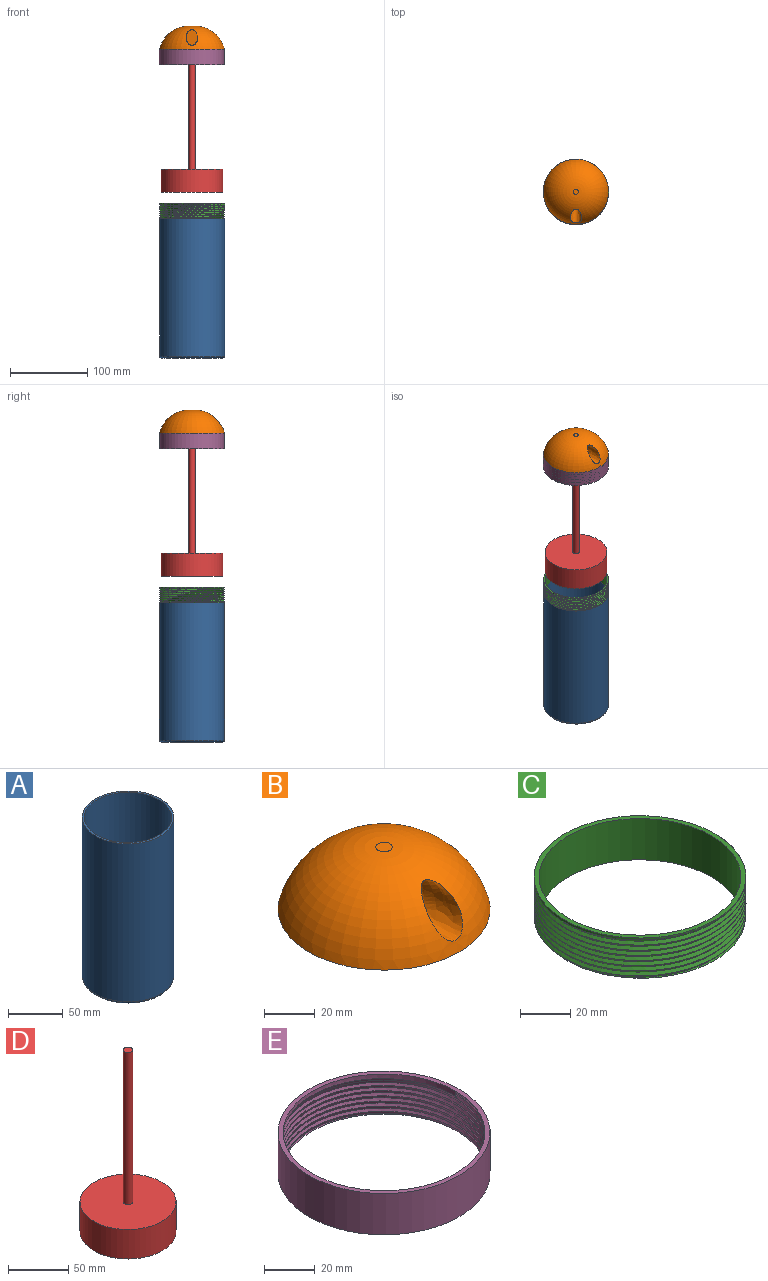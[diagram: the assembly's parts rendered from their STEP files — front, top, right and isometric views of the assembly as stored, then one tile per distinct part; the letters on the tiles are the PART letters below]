
ASSEMBLY  parts=5 mates=3
PART A: 6 faces, bbox 90.9x90.9x180 mm
  f0: cylinder r=42mm len=177.5mm, axis (0,0,1), area 46841.1mm2, adj f2,f5
  f1: plane 79x79mm, normal (0,0,-1), area 4901.7mm2, adj f5
  f2: plane 84x84mm, normal (0,0,1), area 515.2mm2, adj f0,f3
  f3: cylinder r=40mm len=176mm, axis (0,0,1), area 44233.6mm2, adj f2,f4
  f4: plane 80x80mm, normal (0,0,1), area 5026.5mm2, adj f3
  f5: torus R=39.5mm, axis (0,0,1), area 1013.9mm2, adj f0,f1
PART B: 5 faces, bbox 84x84x30 mm
  f0: torus R=3.27mm, axis (0,0,-1), area 8304.5mm2, adj f1,f2,f3
  f1: plane 6.54x6.54mm, normal (0,0,1), area 33.6mm2, adj f0
  f2: plane 84x84mm, normal (0,0,-1), area 5541.8mm2, adj f0
  f3: extruded ~40.32x20mm, area 1802.4mm2, adj f0,f4
  f4: plane 20x15mm, normal (0,-1,0), area 235.6mm2, adj f3
PART C: 7 faces, bbox 84x97x21.7 mm
  f0: cylinder r=42mm len=84mm, axis (0,0,-1), area 90.1mm2, adj f1,f2,f3,f4,f5
  f1: plane 84x84mm, normal (0,0,1), area 515.2mm2, adj f0,f6
  f2: plane 83.05x83.04mm, normal (0,0,-1), area 388.8mm2, adj f0,f3,f4,f6
  f3: bspline ~97x84mm, area 3202.5mm2, adj f0,f2,f4,f5
  f4: bspline ~97x84mm, area 3001.3mm2, adj f0,f2,f3,f5
  f5: plane 2.49x0.97mm, normal (0,-1,0), area 1.2mm2, adj f0,f3,f4
  f6: cylinder r=40mm len=80mm, axis (0,0,-1), area 5026.5mm2, adj f1,f2
PART D: 5 faces, bbox 80x80x185 mm
  f0: cylinder r=40mm len=80mm, axis (0,0,-1), area 7539.8mm2, adj f1,f2
  f1: plane 80x80mm, normal (0,0,1), area 4976.3mm2, adj f0,f3
  f2: plane 80x80mm, normal (0,0,-1), area 5026.5mm2, adj f0
  f3: cylinder r=4mm len=155mm, axis (0,0,-1), area 3895.6mm2, adj f1,f4
  f4: plane 8x8mm, normal (0,0,1), area 50.3mm2, adj f3
PART E: 8 faces, bbox 85x95.7x22.7 mm
  f0: cylinder r=42mm len=84mm, axis (0,0,-1), area 5277.9mm2, adj f1,f2
  f1: plane 84x84mm, normal (0,0,1), area 515.2mm2, adj f0,f3
  f2: plane 85.04x85.04mm, normal (0,0,-1), area 332.7mm2, adj f0,f4,f5
  f3: cylinder r=40mm len=80mm, axis (0,0,-1), area 314.2mm2, adj f1,f6,f7
  f4: bspline ~94.62x81.94mm, area 2561.2mm2, adj f2,f5,f6,f7
  f5: bspline ~94.62x81.94mm, area 2271.2mm2, adj f2,f4,f6
  f6: plane 3.71x0.97mm, normal (0,-1,0), area 1.8mm2, adj f3,f4,f5,f7
  f7: bspline ~93.46x80.94mm, area 328mm2, adj f3,f4,f6
PLACE A t=(6.07,-29.24,-157.87)mm
PLACE B t=(5.95,-29.27,60.94)mm
PLACE C t=(6.07,-29.24,-157.87)mm
PLACE D t=(5.95,-29.27,-124.06)mm
PLACE E t=(5.95,-29.27,40.94)mm
MATE fastened A.f0 <-> C.f0  axis (0,0,1) through (6.07,-29.24,-157.87)mm
MATE fastened D.f0 <-> B.f0  axis (0,0,1) through (5.95,-29.27,60.94)mm
MATE fastened E.f0 <-> B.f0  axis (0,0,-1) through (5.95,-29.27,60.94)mm
